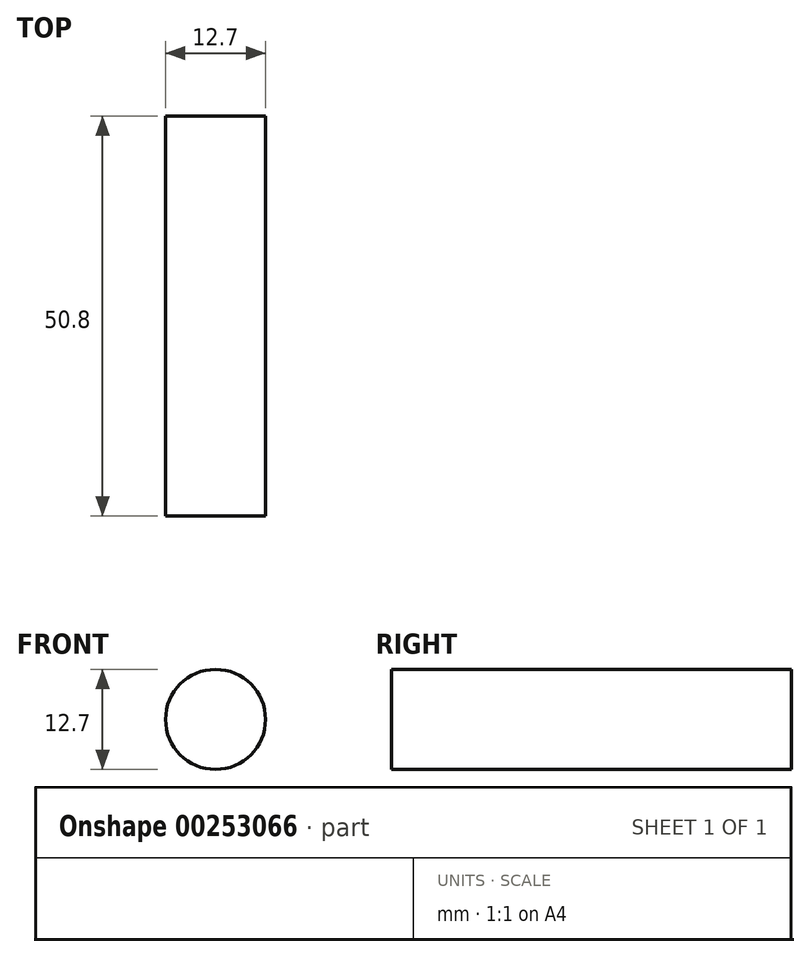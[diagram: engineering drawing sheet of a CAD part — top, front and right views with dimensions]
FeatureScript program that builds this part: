
annotation { "Feature Type Name" : "Feature", "Feature Type Description" : "" }
export const myFeature = defineFeature(function(context is Context, id is Id, definition is map)
    precondition{}
    {
        {
            var Q0;
            Q0=qCreatedBy(makeId("Right.planeOp"),FACE);
            var sketch = newSketch(context, id + "F0", { "sketchPlane" : qUnion([Q0])});
            skLineSegment(sketch, "E0.bottom", {"start": v(14.66, 61.1) * mm, "end": v(-36.14, 61.1) * mm});
            skLineSegment(sketch, "E0.top", {"start": v(14.66, 10.3) * mm, "end": v(-36.14, 10.3) * mm});
            skLineSegment(sketch, "E0.left", {"start": v(14.66, 61.1) * mm, "end": v(14.66, 10.3) * mm});
            skLineSegment(sketch, "E0.right", {"start": v(-36.14, 61.1) * mm, "end": v(-36.14, 10.3) * mm});
            skSolve(sketch);
        }
        {
            var Q0;
            Q0=makeQuery(id+"F0.imprint","IMPRINT",FACE,{"disambiguationData":[TD([[makeQuery(id+"F0.imprint","IMPRINT",EDGE,{"derivedFrom":sQuery(id+"F0.wireOp",EDGE,"E0.bottom")}),1.0]])]});
            extrude(context, id + "F1", {"entities" : qUnion([Q0]), "oppositeDirection" : true, "depth" : 50.8 * mm});
        }
        {
            var Q0;
            Q0=makeQuery(id+"F1.opExtrude","SWEPT_FACE",FACE,{"disambiguationData":[OSD([sQuery(id+"F0.wireOp",EDGE,"E0.right")])]});
            var sketch = newSketch(context, id + "F2", { "sketchPlane" : qUnion([Q0])});
            skLineSegment(sketch, "E1", {"start": v(-50.8, 35.7) * mm, "end": v(0, 35.7) * mm, "construction": true});
            skLineSegment(sketch, "E2", {"start": v(-25.4, 61.1) * mm, "end": v(-25.4, 10.3) * mm});
            skCircle(sketch, "E3", {"center": v(-25.4, 35.7) * mm, "radius": 6.35 * mm});
            skSolve(sketch);
        }
        {
            var Q0;
            {var subQ0=sQuery(id+"F2.wireOp",EDGE,"E3");var subQ1=sQuery(id+"F2.wireOp",EDGE,"E2");var subQ2=makeQuery(id+"F2.imprint","INTERSECT",VERTEX,{"disambiguationData":[OD(0.0)],"derivedFrom":[subQ1,subQ0]});Q0=makeQuery(id+"F2.imprint","IMPRINT",FACE,{"disambiguationData":[TD([[makeQuery(id+"F2.imprint","IMPRINT",EDGE,{"disambiguationData":[TD([[subQ2,-1.0]])],"derivedFrom":subQ1}),-1.0]])]});}
            var Q1;
            {var subQ0=sQuery(id+"F2.wireOp",EDGE,"E3");var subQ1=sQuery(id+"F2.wireOp",EDGE,"E2");var subQ2=makeQuery(id+"F2.imprint","INTERSECT",VERTEX,{"disambiguationData":[OD(0.0)],"derivedFrom":[subQ1,subQ0]});Q1=makeQuery(id+"F2.imprint","IMPRINT",FACE,{"disambiguationData":[TD([[makeQuery(id+"F2.imprint","IMPRINT",EDGE,{"disambiguationData":[TD([[subQ2,-1.0]])],"derivedFrom":subQ1}),1.0]])]});}
            var Q2;
            Q2=sQuery(id+"F2.wireOp",EDGE,"E3");
            extrude(context, id + "F3", {"entities" : qUnion([Q0, Q1]), "operationType" : NewBodyOperationType.REMOVE, "surfaceEntities" : qUnion([Q2]), "endBound" : BoundingType.UP_TO_NEXT, "oppositeDirection" : true, "depth" : 50.8 * mm});
        }
    });
